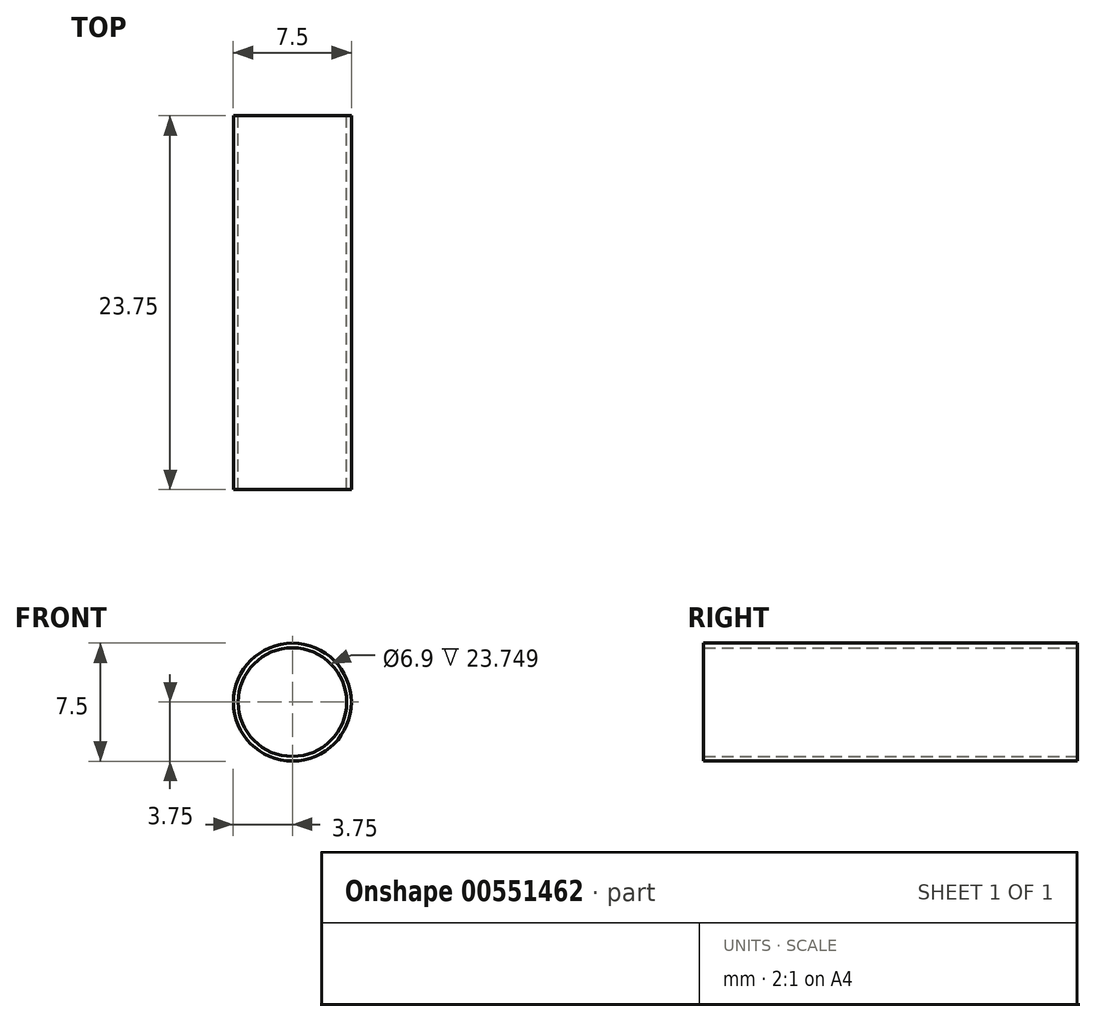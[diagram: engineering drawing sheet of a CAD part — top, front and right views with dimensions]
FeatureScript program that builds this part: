
annotation { "Feature Type Name" : "Feature", "Feature Type Description" : "" }
export const myFeature = defineFeature(function(context is Context, id is Id, definition is map)
    precondition{}
    {
        {
            var Q0;
            Q0=qCreatedBy(makeId("Front.planeOp"),FACE);
            var sketch = newSketch(context, id + "F0", { "sketchPlane" : qUnion([Q0])});
            skCircle(sketch, "E0", {"center": v(0, 0) * mm, "radius": 3.75 * mm});
            skSolve(sketch);
        }
        {
            var Q0;
            Q0=makeQuery(id+"F0.imprint","IMPRINT",FACE,{"disambiguationData":[TD([[makeQuery(id+"F0.imprint","IMPRINT",EDGE,{"derivedFrom":sQuery(id+"F0.wireOp",EDGE,"E0")}),1.0]])]});
            extrude(context, id + "F1", {"entities" : qUnion([Q0]), "depth" : 23.75 * mm, "offsetDistance" : 25.4 * mm});
        }
        {
            var Q0;
            Q0=makeQuery(id+"F1.opExtrude","CAP_FACE",FACE,{"disambiguationData":[OSD([sQuery(id+"F0.wireOp",EDGE,"E0")])],"isStart":true});
            var sketch = newSketch(context, id + "F2", { "sketchPlane" : qUnion([Q0])});
            skCircle(sketch, "E1", {"center": v(0, 0) * mm, "radius": 3.45 * mm});
            skSolve(sketch);
        }
        {
            var Q0;
            Q0=makeQuery(id+"F2.imprint","IMPRINT",FACE,{"disambiguationData":[TD([[makeQuery(id+"F2.imprint","IMPRINT",EDGE,{"derivedFrom":sQuery(id+"F2.wireOp",EDGE,"E1")}),1.0]])]});
            extrude(context, id + "F3", {"entities" : qUnion([Q0]), "operationType" : NewBodyOperationType.REMOVE, "oppositeDirection" : true, "depth" : 25.4 * mm, "offsetDistance" : 25.4 * mm});
        }
    });
